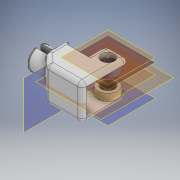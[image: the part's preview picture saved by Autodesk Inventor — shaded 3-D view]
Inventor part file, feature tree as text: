
AUTODESK INVENTOR PART (.ipt)
format: ipt  version: 2020 (Build 240168000, 168)  size: 444,928 bytes
history: native  units: mm
features: sketch x18, extrude x16, plane x8, projected_geometry x6, fillet x4, mirror x3, chamfer x1
ambient origin geometry x8: Origin, YZ Plane, XZ Plane, XY Plane, X Axis, Y Axis, Z Axis, Center Point
bodies: Solid1 (feature_tree)
feature tree (56):
  plane  "Work Plane2"
  sketch  "Sketch5"  dims[d8=0.5mm d9=0.5mm d18=6.0mm d33=7.5mm]
  plane  "Work Plane3"
  extrude  "Extrusion4"  Depth=7.5mm
  plane  "Work Plane5"
  extrude  "Extrusion5"  Depth=11.0mm
  plane  "Work Plane1"
  plane  "Work Plane4"
  extrude  "Extrusion6"  Depth=2.0mm
  plane  "Work Plane6"
  extrude  "Extrusion7"  Depth=2.0mm
  extrude  "Extrusion8"  Depth=9.0mm
  plane  "Work Plane7"
  sketch  "Sketch13"  dims[d45=13.0mm d46=2.5mm]
  extrude  "Extrusion9"  Depth=2.5mm
  sketch  "Sketch14"  dims[d47=5.0mm d48=2.0mm d49=0.0mm]
  extrude  "Extrusion10"  Depth=2.0mm TaperAngle=0.0deg
  extrude  "Extrusion11"  Depth=7.0mm
  extrude  "Extrusion12"  Depth=1.0mm
  extrude  "Extrusion13"  Depth=1.0mm TaperAngle=0.0deg
  fillet  "Fillet14"  Radius=3.5mm
  mirror  "Mirror4"
  extrude  "Extrusion14"  Depth=10.0mm TaperAngle=0.0deg
  mirror  "Mirror5"
  extrude  "Extrusion15"  Depth=2.0mm
  fillet  "Fillet15"  Radius=2.0mm
  extrude  "Extrusion16"  Depth=1.0mm TaperAngle=0.0deg
  extrude  "Extrusion17"  Depth=2.0mm
  sketch  "Sketch24"  dims[d89=1.5mm d90=0.0mm d91=2.0mm d92=10.5mm d93=1.0mm d94=0.0mm]
  chamfer  "Chamfer1"  Distance=3.25mm
  extrude  "Extrusion18"  Depth=2.0mm
  fillet  "Fillet16"  Radius=10.5mm
  fillet  "Fillet17"  Radius=1.0mm
  extrude  "Extrusion19"  Depth=2.0mm TaperAngle=45.0deg
  mirror  "Mirror6"
  sketch  "Sketch6"  dims[d34=7.5mm d35=11.0mm]
  sketch  "Sketch7"  dims[d36=7.5mm d37=2.0mm]
  sketch  "Sketch10"  dims[d38=2.0mm d39=0.0mm d41=2.0mm]
  projected_geometry  "Projected Loop1"
  sketch  "Sketch12"  dims[d42=6.26mm d43=0.0mm d44=9.0mm]
  projected_geometry  "Projected Loop2"
  sketch  "Sketch15"  dims[d51=6.0mm d52=7.0mm]
  sketch  "Sketch17"  dims[d53=1.0mm d55=1.0mm]
  projected_geometry  "Projected Loop3"
  sketch  "Sketch18"  dims[d56=6.25mm d57=0.0mm d59=1.0mm d60=0.0mm d61=3.5mm]
  projected_geometry  "Projected Loop4"
  sketch  "Sketch19"  dims[d62=10.0mm d68=7.0mm d69=0.0mm]
  projected_geometry  "Projected Loop5"
  plane  "Work Plane8"
  sketch  "Sketch20"  dims[d75=2.0mm d76=0.0mm d77=6.0mm d78=2.0mm d79=0.0mm]
  sketch  "Sketch21"  dims[d80=1.0mm d81=0.0mm d82=1.0mm d83=0.0mm]
  sketch  "Sketch22"  dims[d84=2.0mm d85=5.0mm]
  sketch  "Sketch23"  dims[d86=7.0mm d87=3.25mm d88=0.0mm]
  sketch  "Sketch25"  dims[d95=6.0mm d96=0.0mm d97=0.8mm d98=2.0mm d99=45.0deg]
  projected_geometry  "Projected Loop6"
  sketch  "Sketch26"  dims[d100=13.0mm d101=1.0mm d102=0.0mm d103=2.0mm d104=2.0mm d105=9.0mm d106=2.0mm d107=0.0mm d15=0.5mm d16=0.872665mm d17=0.5mm d50=0.5mm]
